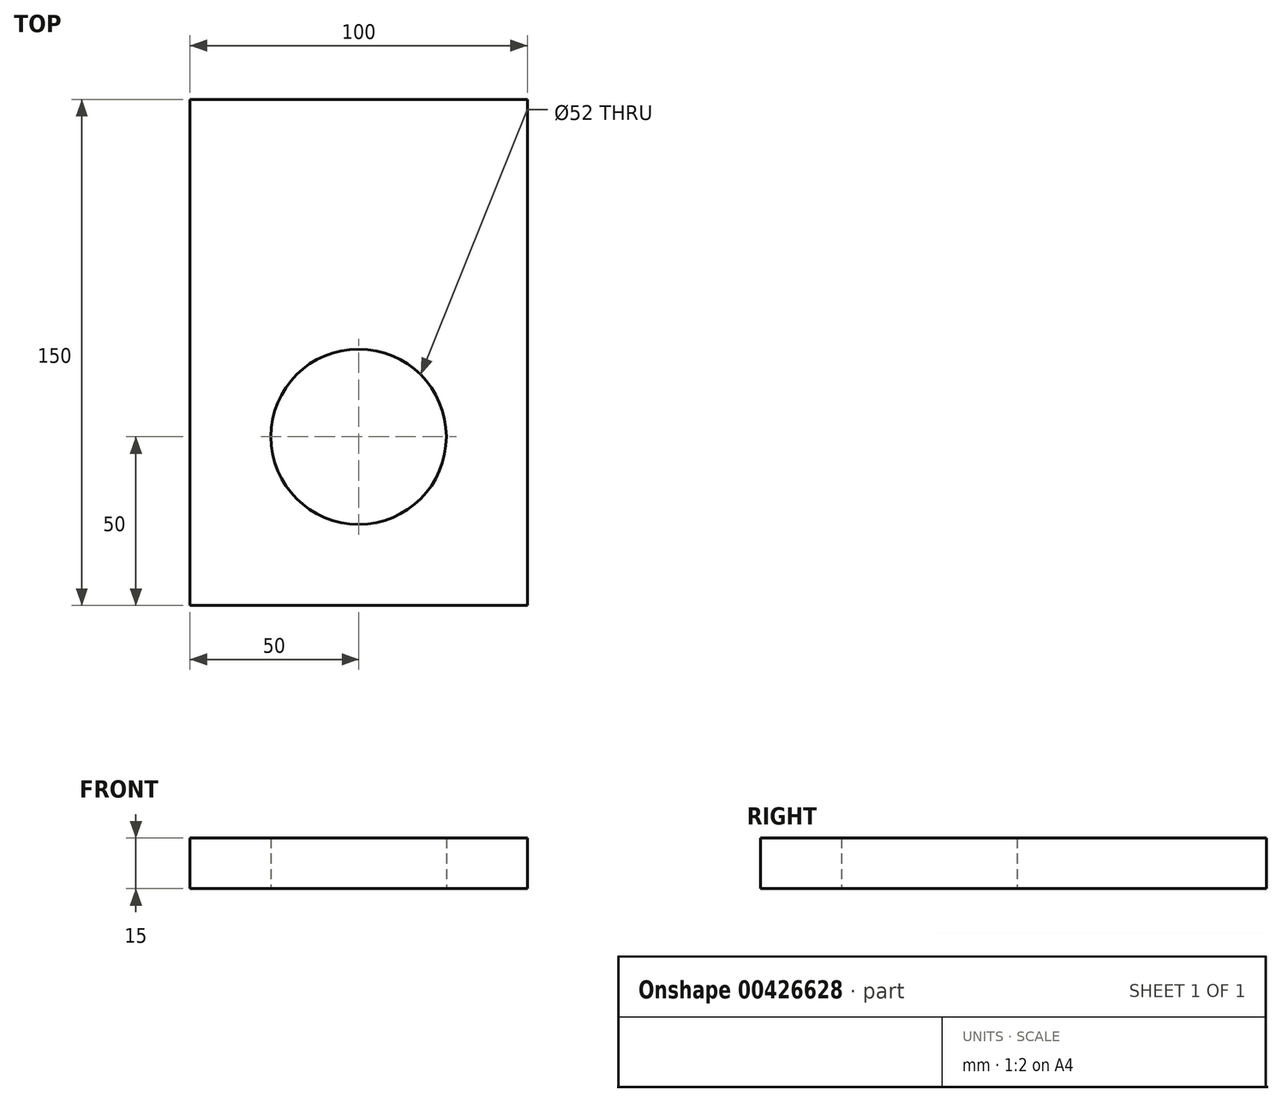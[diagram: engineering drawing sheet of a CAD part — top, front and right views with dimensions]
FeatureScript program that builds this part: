
annotation { "Feature Type Name" : "Feature", "Feature Type Description" : "" }
export const myFeature = defineFeature(function(context is Context, id is Id, definition is map)
    precondition{}
    {
        {
            var Q0;
            Q0=qCreatedBy(makeId("Top.planeOp"),FACE);
            var sketch = newSketch(context, id + "F0", { "sketchPlane" : qUnion([Q0])});
            skLineSegment(sketch, "E0.bottom", {"start": v(0, 0) * mm, "end": v(100, 0) * mm});
            skLineSegment(sketch, "E0.top", {"start": v(0, 150) * mm, "end": v(100, 150) * mm});
            skLineSegment(sketch, "E0.left", {"start": v(0, 0) * mm, "end": v(0, 150) * mm});
            skLineSegment(sketch, "E0.right", {"start": v(100, 0) * mm, "end": v(100, 150) * mm});
            skCircle(sketch, "E1", {"center": v(50, 50) * mm, "radius": 26 * mm});
            skSolve(sketch);
        }
        {
            var Q0;
            Q0=makeQuery(id+"F0.imprint","IMPRINT",FACE,{"disambiguationData":[TD([[makeQuery(id+"F0.imprint","IMPRINT",EDGE,{"derivedFrom":sQuery(id+"F0.wireOp",EDGE,"E0.bottom")}),1.0]])]});
            extrude(context, id + "F1", {"entities" : qUnion([Q0]), "depth" : 15 * mm});
        }
    });
